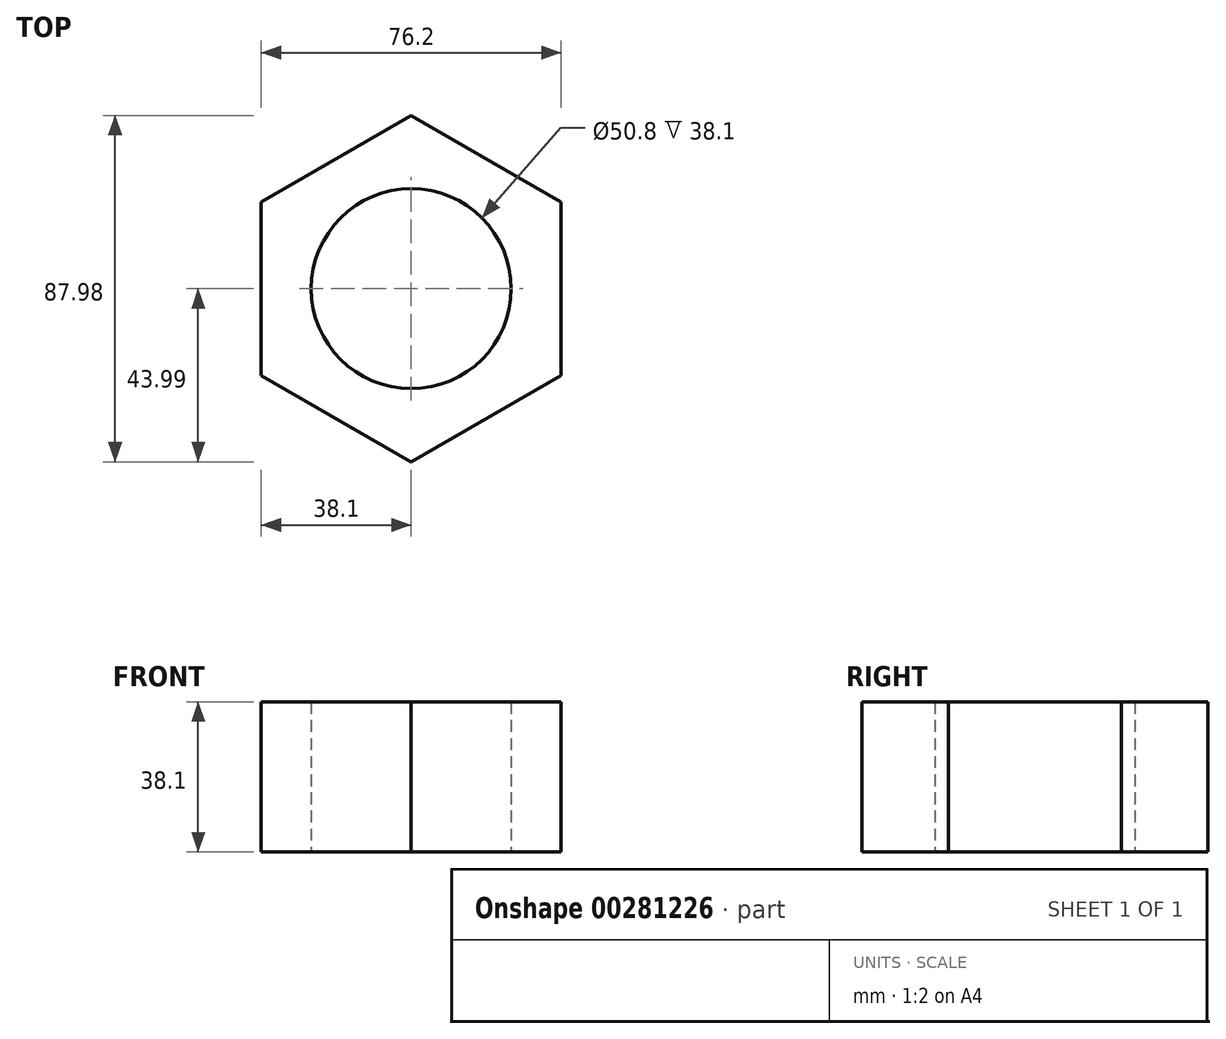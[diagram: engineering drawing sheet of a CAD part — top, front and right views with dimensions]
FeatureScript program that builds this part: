
annotation { "Feature Type Name" : "Feature", "Feature Type Description" : "" }
export const myFeature = defineFeature(function(context is Context, id is Id, definition is map)
    precondition{}
    {
        {
            var Q0;
            Q0=qCreatedBy(makeId("Top.planeOp"),FACE);
            var sketch = newSketch(context, id + "F0", { "sketchPlane" : qUnion([Q0])});
            skCircle(sketch, "E0.cCircle", {"center": v(0, 0) * mm, "radius": 38.1 * mm, "construction": true});
            skLineSegment(sketch, "E0.0", {"start": v(-38.1, -22) * mm, "end": v(-38.1, 22) * mm});
            skLineSegment(sketch, "E0.1", {"start": v(-38.1, 22) * mm, "end": v(0, 44) * mm});
            skLineSegment(sketch, "E0.2", {"start": v(0, 44) * mm, "end": v(38.1, 22) * mm});
            skLineSegment(sketch, "E0.3", {"start": v(38.1, 22) * mm, "end": v(38.1, -22) * mm});
            skLineSegment(sketch, "E0.4", {"start": v(38.1, -22) * mm, "end": v(0, -44) * mm});
            skLineSegment(sketch, "E0.5", {"start": v(0, -44) * mm, "end": v(-38.1, -22) * mm});
            skPoint(sketch, "E0.0.midPoint", {"position": v(-38.1, 0) * mm});
            skCircle(sketch, "E1", {"center": v(0, 0) * mm, "radius": 25.4 * mm});
            skSolve(sketch);
        }
        {
            var Q0;
            Q0 = qSketchRegion(id + "F0", true);
            extrude(context, id + "F1", {"entities" : qUnion([Q0]), "depth" : 38.1 * mm});
        }
    });
